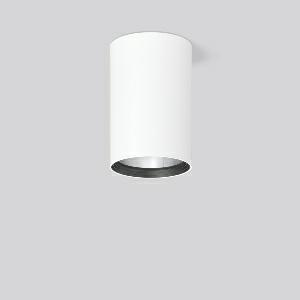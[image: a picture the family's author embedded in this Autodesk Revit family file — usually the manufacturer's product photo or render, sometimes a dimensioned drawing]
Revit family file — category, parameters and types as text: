
# Revit family: heledon_maxi_a_931218_002_76_cea1
name_source: partatom
category: Lighting Fixtures
units: mm (PartAtom-declared; Revit-internal decimal feet)

## family parameters
Cut with Voids When Loaded = No
Host = Face
Light Source = No
Part Type = Normal
Room Calculation Point = No
Round Connector Dimension = Use Diameter
Shared = No

## types (1)
- HELEDON maxi A (1 x LED Modul 930, 3350 lm, 3000)
    Apparent Load = 25 VA
    Approval mark = CE
    CIE Flux Codes = 100 100 100 100 100
    Color Rendering = 90
    Color Temperature = 3000
    Default Elevation = 1800 mm
    Description = Series: HELEDON maxi
Cylindrical surface-mounted downlight. Housing: die-cast aluminium, powder-coated. Internal ceiling frame polycarbonate with bayonet mounting. Black plastic ring and recessed LED to prevent glare from the side. Optical assembly with reflector made of MIRO-Silver with 98% total light reflection for outstanding efficiency - can be changed without tools. Best colour rendering index Ra>90. Suitable for Ceiling mounting. Easy installation with a separate ceiling frame with bayonet mounting and plug connection. Driver integrated. Connected via plug-in connector. High quality converter without flickering and stroboscopic effect. The following accessories can be mounted without use of tools: interchangeable lenses, decorative glasses, honeycomb louvre, clear and frosted diffusers, white interchangeable plastic ring. 
Colour: traffic white, matt (RAL 9016)
Diameter: 123 mm
Height: 183 mm
Lamp: LED
Socket: without socket
Colour temperature: 3000K
Colour rendering index (CRI): 92
System power: 25 W
Rated luminous flux: 3350 lm
Luminous efficiency: 134 lm/W
Control gear: Converter, dimmable, DALI
Protection class: I
Type of protection: IP 20
    Height = 183 mm
    Lamp = 1 x LED Modul 930
    Lamp Light Flux = 3350 lm
    Lamp count = 1
    Length = 123 mm
    Lifetime = 50000 h
    Luminous efficacy = 134 lm/W
    Manufacturer = RZB
    ModVariant = No
    Model = 931218.002.76
    Mounting Place = Ceiling
    Mounting Type = Surface mounted
    Number of Poles = 1
    OnlyDefault = Yes
    Power Factor = 1
    Product Name = HELEDON maxi A
    Product group = Surface mounted downlights
    ProductGroupID = 302
    Protection Class = Protection class I
    Protection Degree = IP 20
    RLX_Detail_Level = 1
    RLX_Emergency_Light_Flux = 0 lm
    RLX_Emergency_Type = 0
    RLX_Emergency_Type_DB = No
    RlxData = <blob elided: 96381 chars, md5=0ea90169>
    Socket = socket
    Standby Power = 0 W
    System Light Flux = 3350 lm
    System Power = 25 W
    Type Comments = Product without accessories
    Type Image = 931192.002.jpg
    URL = http://relux.com
    VarID = ---
    Voltage = 230 V
    Voltage Range = 220-240 V
    Weight = 0.00 kg
    Width = 0 mm  [stored 0 ft]

note: [stored X ft] marks values corroborated as IEEE doubles in the binary element streams (Revit-internal decimal feet)

## geometry (parser evidence)
native form markers: Blend x4, Sweep x9
no freeform markers — native parametric forms only
